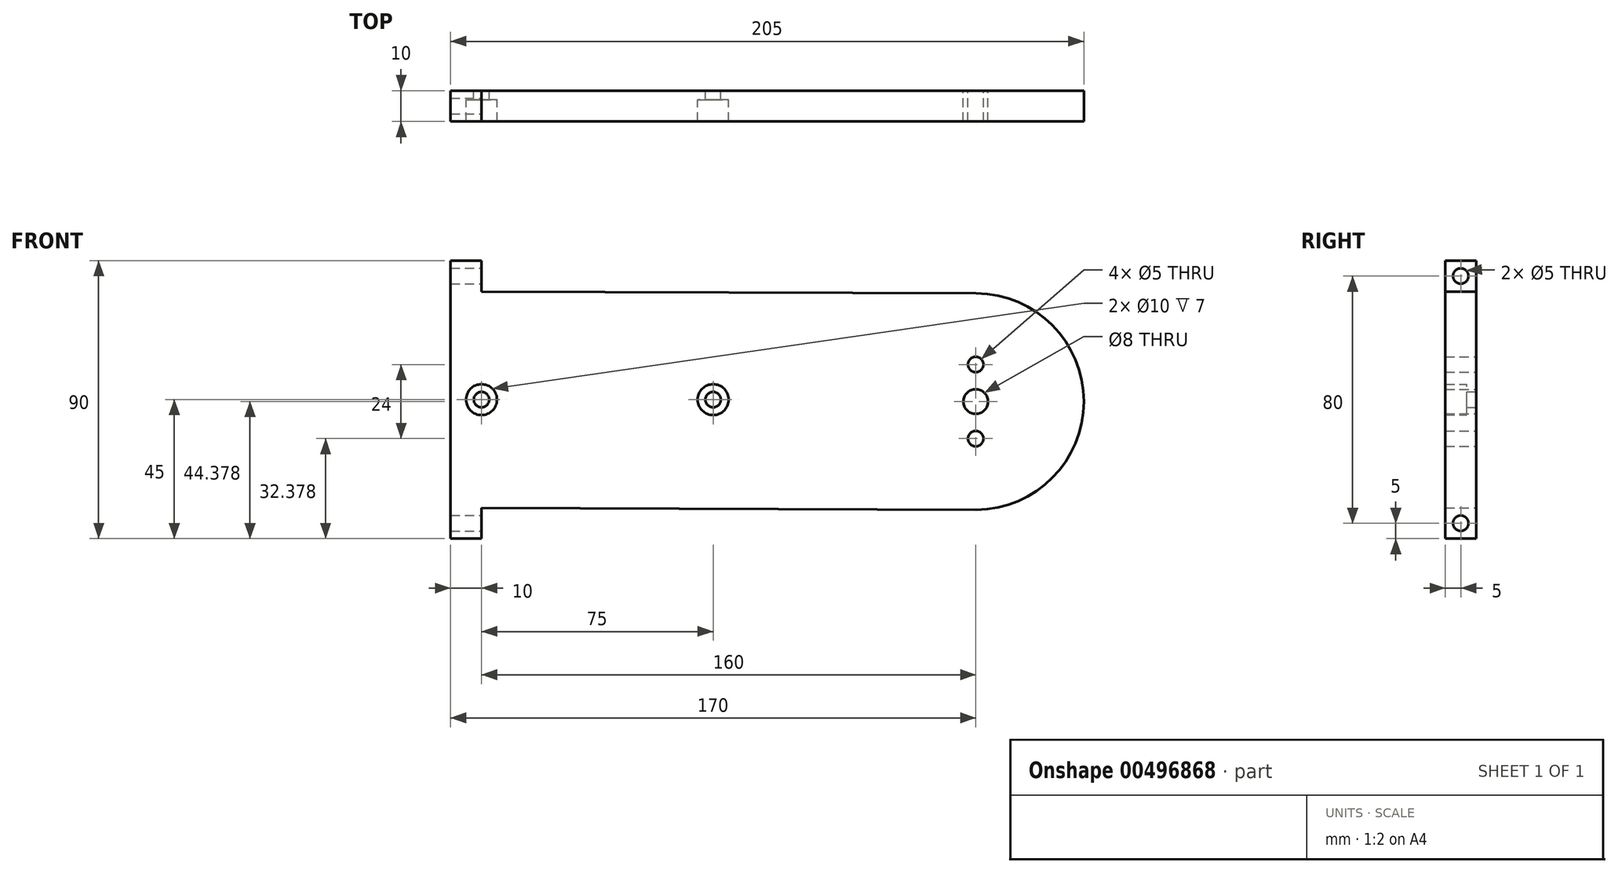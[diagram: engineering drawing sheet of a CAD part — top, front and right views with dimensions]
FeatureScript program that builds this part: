
annotation { "Feature Type Name" : "Feature", "Feature Type Description" : "" }
export const myFeature = defineFeature(function(context is Context, id is Id, definition is map)
    precondition{}
    {
        {
            var Q0;
            Q0=qCreatedBy(makeId("Front.planeOp"),FACE);
            var sketch = newSketch(context, id + "F0", { "sketchPlane" : qUnion([Q0])});
            skPoint(sketch, "E0.middle", {"position": v(0, 0) * mm});
            skLineSegment(sketch, "E1", {"start": v(-85, 45) * mm, "end": v(-75, 45) * mm});
            skLineSegment(sketch, "E2", {"start": v(-75, 45) * mm, "end": v(-75, 35) * mm});
            skLineSegment(sketch, "E3", {"start": v(-85, -45) * mm, "end": v(-75, -45) * mm});
            skLineSegment(sketch, "E4", {"start": v(-75, -45) * mm, "end": v(-75, -35) * mm});
            skLineSegment(sketch, "E5", {"start": v(-75, 35) * mm, "end": v(85.14, 34.38) * mm});
            skLineSegment(sketch, "E6", {"start": v(-75, -35) * mm, "end": v(85.14, -35.62) * mm});
            skArc(sketch, "E7", {"start": v(85.14, 34.38) * mm, "mid": v(120, -0.62) * mm, "end": v(85.14, -35.62) * mm});
            skCircle(sketch, "E8", {"center": v(85, -0.62) * mm, "radius": 4 * mm});
            skLineSegment(sketch, "E9", {"start": v(85, -0.62) * mm, "end": v(85, 11.38) * mm});
            skLineSegment(sketch, "E10", {"start": v(85, -0.62) * mm, "end": v(85, -12.62) * mm});
            skCircle(sketch, "E11", {"center": v(85, 11.38) * mm, "radius": 2.5 * mm});
            skCircle(sketch, "E12", {"center": v(85, -12.62) * mm, "radius": 2.5 * mm});
            skLineSegment(sketch, "E13", {"start": v(-85, 45) * mm, "end": v(-85, -45) * mm});
            skCircle(sketch, "E14", {"center": v(-75, 0) * mm, "radius": 2.5 * mm});
            skCircle(sketch, "E15", {"center": v(-75, 0) * mm, "radius": 5 * mm});
            skCircle(sketch, "E16", {"center": v(0, 0) * mm, "radius": 2.5 * mm});
            skCircle(sketch, "E17", {"center": v(0, 0) * mm, "radius": 5 * mm});
            skSolve(sketch);
        }
        {
            var Q0;
            Q0 = qSketchRegion(id + "F0", true);
            extrude(context, id + "F1", {"entities" : qUnion([Q0]), "depth" : 10 * mm});
        }
        {
            var Q0;
            Q0=makeQuery(id+"F1.opExtrude","SWEPT_FACE",FACE,{"disambiguationData":[OSD([sQuery(id+"F0.wireOp",EDGE,"E2")])]});
            var sketch = newSketch(context, id + "F2", { "sketchPlane" : qUnion([Q0])});
            skCircle(sketch, "E18", {"center": v(-5, 40) * mm, "radius": 2.5 * mm});
            skSolve(sketch);
        }
        {
            var Q0;
            Q0 = qSketchRegion(id + "F2", true);
            extrude(context, id + "F3", {"entities" : qUnion([Q0]), "operationType" : NewBodyOperationType.REMOVE, "oppositeDirection" : true, "depth" : 25 * mm});
        }
        {
            var Q0;
            Q0=makeQuery(id+"F1.opExtrude","SWEPT_FACE",FACE,{"disambiguationData":[OSD([sQuery(id+"F0.wireOp",EDGE,"E4")])]});
            var sketch = newSketch(context, id + "F4", { "sketchPlane" : qUnion([Q0])});
            skCircle(sketch, "E19", {"center": v(-5, -40) * mm, "radius": 2.5 * mm});
            skSolve(sketch);
        }
        {
            var Q0;
            Q0 = qSketchRegion(id + "F4", true);
            extrude(context, id + "F5", {"entities" : qUnion([Q0]), "operationType" : NewBodyOperationType.REMOVE, "oppositeDirection" : true, "depth" : 25 * mm});
        }
        {
            var Q0;
            Q0=makeQuery(id+"F0.imprint","IMPRINT",FACE,{"disambiguationData":[TD([[makeQuery(id+"F0.imprint","IMPRINT",EDGE,{"derivedFrom":sQuery(id+"F0.wireOp",EDGE,"E14")}),-1.0]])]});
            var Q1;
            Q1=makeQuery(id+"F0.imprint","IMPRINT",FACE,{"disambiguationData":[TD([[makeQuery(id+"F0.imprint","IMPRINT",EDGE,{"derivedFrom":sQuery(id+"F0.wireOp",EDGE,"E16")}),-1.0]])]});
            extrude(context, id + "F6", {"entities" : qUnion([Q0, Q1]), "operationType" : NewBodyOperationType.ADD, "depth" : 3 * mm});
        }
    });
